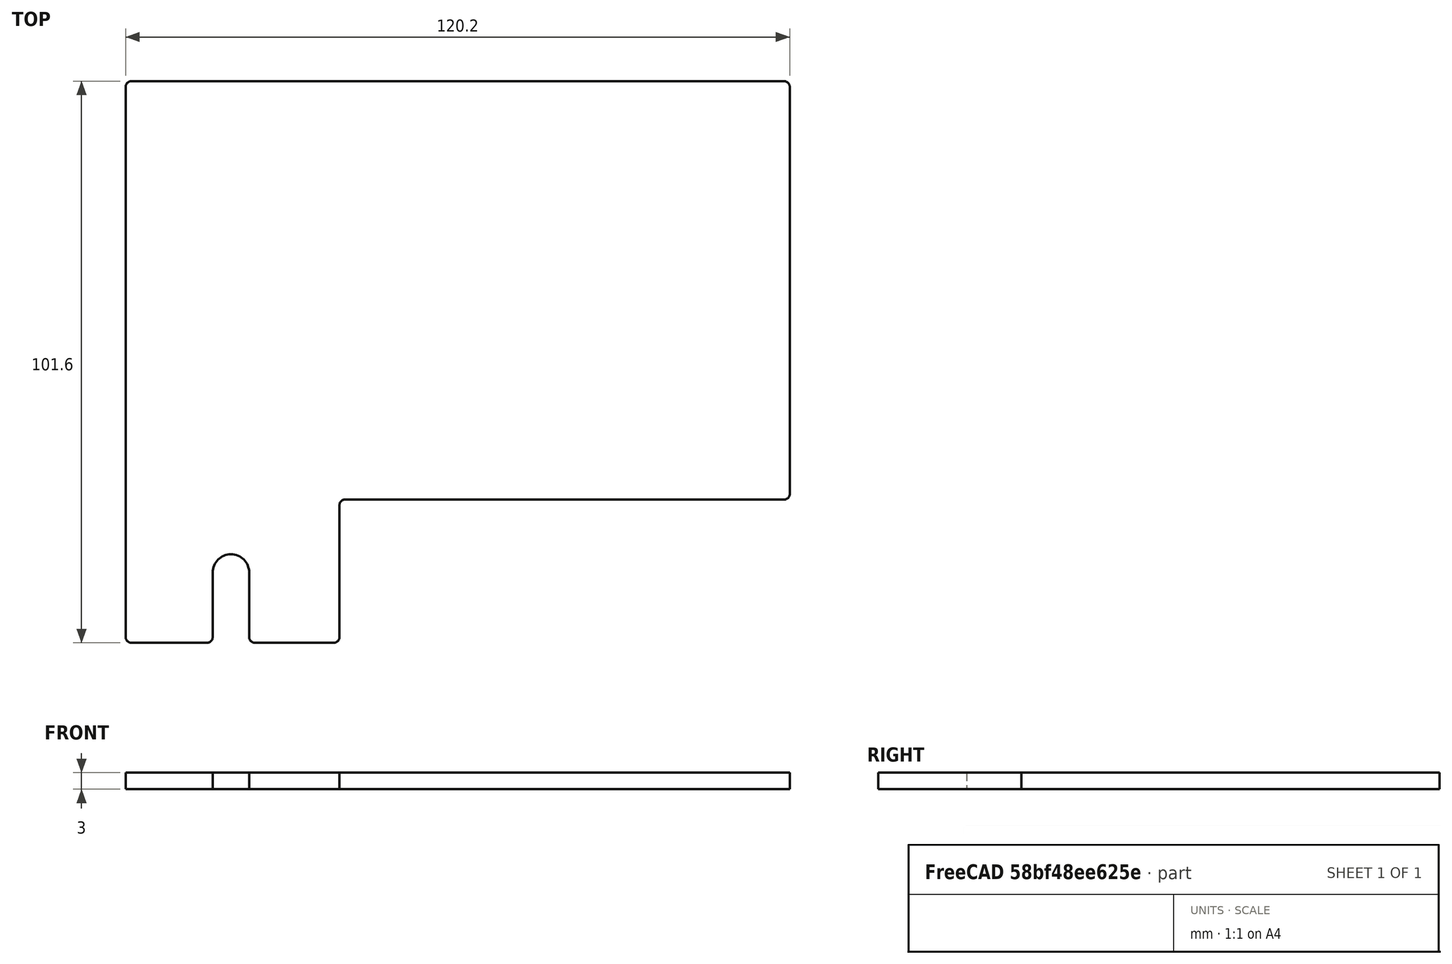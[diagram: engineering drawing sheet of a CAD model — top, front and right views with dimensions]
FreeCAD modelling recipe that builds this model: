
FCSTD DOCUMENT  (FreeCAD 0.21R33675 (Git))
Label: right_wall_front
License: All rights reserved
LicenseURL: http://en.wikipedia.org/wiki/All_rights_reserved
objects: Spreadsheet::Sheet×1, Sketcher::SketchObject×1, PartDesign::Pad×1, PartDesign::Body×1
note: 4 computed .brp shape members not serialized (recipe doc carries the construction recipe); baked Part::Feature solids carry a one-line shape summary decoded from their .brp

FEATURE [Spreadsheet::Sheet] Spreadsheet
  cells = A2='Parameters; A3='Thickness; B3(Thickness)==3 mm; A4='BeamLength; B4(BeamLength)==18 in; A5='BracketLength; B5(BracketLength)==108.6 mm; A6='DistanceLeftBracketEdgeToDoor; B6(DistanceLeftBracketEdgeToDoor)==82.4999 mm; A7='DistanceRightBracketEdgeToDoor; B7(DistanceRightBracketEdgeToDoor)==23.1001 mm; A8='ServoOffsetFromCenter; B8(ServoOffsetFromCenter)==3 in + 1 * (DistanceLeftBracketEdgeToDoor - DistanceRightBracketEdgeToDoor); A9='DoorMargin; B9(DoorMargin)==1 mm; A10='LengthMargin; B10(LengthMargin)==0 mm; A11='LengthLeftBracketEdgeToDoorGap; B11(LengthLeftBracketEdgeToDoorGap)==DistanceLeftBracketEdgeToDoor - DoorMargin; A12='LengthRightBracketEdgeToDoorGap; B12(LengthRightBracketEdgeToDoorGap)==DistanceRightBracketEdgeToDoor - DoorMargin; A13='LengthDoorGap; B13(LengthDoorGap)==BracketLength - LengthLeftBracketEdgeToDoorGap - LengthRightBracketEdgeToDoorGap; A14='BeamLengthMinusBracketLength; B14(BeamLengthMinusBracketLength)==BeamLength - BracketLength; A15='DistanceFrontToDoor; B15(DistanceFrontToDoor)==0.5 * BeamLengthMinusBracketLength + LengthLeftBracketEdgeToDoorGap - ServoOffsetFromCenter; A16='DistanceFrontToBracket; B16(DistanceFrontToBracket)==0.5 * BeamLengthMinusBracketLength - ServoOffsetFromCenter; A17='LengthFrontToDoor; B17(LengthFrontToDoor)==DistanceFrontToDoor - LengthMargin; A18='LengthFrontToBracket; B18(LengthFrontToBracket)==DistanceFrontToBracket - LengthMargin; A19='Height; B19(Height)==4 in; A20='CutoutMargin; B20(CutoutMargin)==0.5 mm; A21='CutoutHeight; B21(CutoutHeight)==1 in + CutoutMargin; A22='FilletRadius; B22(FilletRadius)==1 mm; A23='MountHoleDiameter; B23(MountHoleDiameter)==0.26 in; A24='MountHoleDistanceFromBottom; B24(MountHoleDistanceFromBottom)==0.5 in; A25='MountHoleSideMargin; B25(MountHoleSideMargin)==0.75 in; B27==3 in + DistanceLeftBracketEdgeToDoor + 0.5 * Thickness - 0.5 * BracketLength
FEATURE [Sketcher::SketchObject] Sketch
  FullyConstrained = true
  MapMode = 5
  Support = -> [XY_Plane]
  expr: Constraints[14] = Spreadsheet.FilletRadius
  expr: Constraints[20] = Spreadsheet.Height
  expr: Constraints[48] = Spreadsheet.MountHoleSideMargin
  expr: Constraints[68] = Spreadsheet.MountHoleDiameter
  expr: Constraints[69] = Spreadsheet.MountHoleDistanceFromBottom
  expr: Constraints[7] = Spreadsheet.LengthFrontToDoor
  expr: Constraints[8] = Spreadsheet.LengthFrontToBracket
  expr: Constraints[9] = Spreadsheet.CutoutHeight
  sketch-geometry (30):
    g0: LineSegment StartX=0 StartY=100.6 StartZ=0 EndX=0 EndY=1 EndZ=0
    g1: LineSegment StartX=1 StartY=0 StartZ=0 EndX=37.7002 EndY=0 EndZ=0
    g2: LineSegment StartX=38.7002 StartY=1 StartZ=0 EndX=38.7002 EndY=24.9 EndZ=0
    g3: LineSegment StartX=39.7002 StartY=25.9 StartZ=0 EndX=119.2 EndY=25.9 EndZ=0
    g4: LineSegment StartX=120.2 StartY=26.9 StartZ=0 EndX=120.2 EndY=100.6 EndZ=0
    g5: LineSegment StartX=119.2 StartY=101.6 StartZ=0 EndX=1 EndY=101.6 EndZ=0
    g6: ArcOfCircle CenterX=1 CenterY=100.6 CenterZ=0 NormalX=0 NormalY=0 NormalZ=1 AngleXU=0 Radius=1 StartAngle=1.5708 EndAngle=3.14159
    g7: GeomPoint X=0 Y=101.6 Z=0
    g8: ArcOfCircle CenterX=1 CenterY=1 CenterZ=0 NormalX=0 NormalY=0 NormalZ=1 AngleXU=0 Radius=1 StartAngle=3.14159 EndAngle=4.71239
    g9: GeomPoint X=0 Y=0 Z=0
    g10: ArcOfCircle CenterX=37.7002 CenterY=1 CenterZ=0 NormalX=0 NormalY=0 NormalZ=1 AngleXU=0 Radius=1 StartAngle=4.71239 EndAngle=6.28319
    g11: GeomPoint X=38.7002 Y=0 Z=0
    g12: ArcOfCircle CenterX=39.7002 CenterY=24.9 CenterZ=0 NormalX=0 NormalY=0 NormalZ=1 AngleXU=0 Radius=1 StartAngle=1.5708 EndAngle=3.14159
    g13: GeomPoint X=38.7002 Y=25.9 Z=0
    g14: ArcOfCircle CenterX=119.2 CenterY=26.9 CenterZ=0 NormalX=0 NormalY=0 NormalZ=1 AngleXU=0 Radius=1 StartAngle=4.71239 EndAngle=6.28319
    g15: GeomPoint X=120.2 Y=25.9 Z=0
    g16: ArcOfCircle CenterX=119.2 CenterY=100.6 CenterZ=0 NormalX=0 NormalY=0 NormalZ=1 AngleXU=0 Radius=1 StartAngle=3.8e-15 EndAngle=1.5708
    g17: GeomPoint X=120.2 Y=101.6 Z=0
    g18: GeomPoint X=19.3501 Y=0 Z=0
    g19: LineSegment StartX=19.05 StartY=0 StartZ=0 EndX=19.05 EndY=12.7 EndZ=0
    g20: Circle CenterX=19.05 CenterY=12.7 CenterZ=0 NormalX=0 NormalY=0 NormalZ=1 AngleXU=0 Radius=3.302
    g21: LineSegment StartX=19.05 StartY=12.7 StartZ=0 EndX=0 EndY=12.7 EndZ=0
    g22: ArcOfCircle CenterX=19.05 CenterY=12.7 CenterZ=0 NormalX=0 NormalY=0 NormalZ=1 AngleXU=0 Radius=3.302 StartAngle=0 EndAngle=3.14159
    g23: LineSegment StartX=19.05 StartY=12.7 StartZ=0 EndX=22.352 EndY=12.7 EndZ=0
    g24: LineSegment StartX=15.748 StartY=12.7 StartZ=0 EndX=15.748 EndY=1 EndZ=0
    g25: LineSegment StartX=22.352 StartY=12.7 StartZ=0 EndX=22.352 EndY=1 EndZ=0
    g26: ArcOfCircle CenterX=14.748 CenterY=1 CenterZ=0 NormalX=0 NormalY=0 NormalZ=1 AngleXU=0 Radius=1 StartAngle=4.71239 EndAngle=6.28319
    g27: ArcOfCircle CenterX=23.352 CenterY=1 CenterZ=0 NormalX=0 NormalY=0 NormalZ=1 AngleXU=0 Radius=1 StartAngle=3.14159 EndAngle=4.71239
    g28: LineSegment StartX=1 StartY=0 StartZ=0 EndX=14.748 EndY=0 EndZ=0
    g29: LineSegment StartX=23.352 StartY=0 StartZ=0 EndX=37.7002 EndY=0 EndZ=0
  constraints (71):
    c: Vertical(g0)
    c: Horizontal(g1)
    c: Vertical(g2)
    c: Horizontal(g3)
    c: Vertical(g4)
    c: Horizontal(g5)
    c: Coincident(g-1,g9)
    c: DistanceX(g7,g17) = 120.2
    c: DistanceX(g9,g11) = 38.7002
    c: DistanceY(g11,g13) = 25.9
    c: PointOnObject(g7,g0)
    c: PointOnObject(g7,g5)
    c: Tangent(g0,g6) = -1.5708
    c: Tangent(g5,g6) = -1.5708
    c: Radius(g6) = 1
    c: PointOnObject(g9,g0)
    c: PointOnObject(g9,g1)
    c: Tangent(g0,g8) = -1.5708
    c: Tangent(g1,g8) = -1.5708
    c: Equal(g8,g6)
    c: DistanceY(g1,g5) = 101.6
    c: PointOnObject(g11,g1)
    c: PointOnObject(g11,g2)
    c: Tangent(g1,g10) = -1.5708
    c: Tangent(g2,g10) = -1.5708
    c: Equal(g10,g8)
    c: PointOnObject(g13,g2)
    c: PointOnObject(g13,g3)
    c: Tangent(g2,g12) = 1.5708
    c: Tangent(g3,g12) = 1.5708
    c: Equal(g12,g10)
    c: PointOnObject(g15,g3)
    c: PointOnObject(g15,g4)
    c: Tangent(g3,g14) = -1.5708
    c: Tangent(g4,g14) = -1.5708
    c: Equal(g14,g12)
    c: PointOnObject(g17,g5)
    c: PointOnObject(g17,g4)
    c: Tangent(g5,g16) = -1.5708
    c: Tangent(g4,g16) = -1.5708
    c: Equal(g16,g14)
    c: Symmetric(g1,g1,g18)
    c: Vertical(g19)
    c: PointOnObject(g19,g1)
    c: Coincident(g20,g19)
    c: Coincident(g21,g20)
    c: PointOnObject(g21,g0)
    c: Horizontal(g21)
    c: DistanceX(g21,g21) = 19.05
    c: Coincident(g22,g19)
    c: PointOnObject(g22,g21)
    c: Coincident(g23,g22)
    c: Coincident(g23,g22)
    c: Horizontal(g23)
    c: PointOnObject(g22,g20)
    c: Coincident(g24,g22)
    c: Vertical(g24)
    c: Coincident(g25,g22)
    c: Vertical(g25)
    c: Equal(g24,g25)
    c: Tangent(g26,g24) = 1.5708
    c: Tangent(g26,g1) = -1.5708
    c: Tangent(g27,g25) = -1.5708
    c: Tangent(g27,g1) = -1.5708
    c: Equal(g26,g8)
    c: Coincident(g28,g8)
    c: Coincident(g28,g26)
    c: Coincident(g29,g27)
    c: Diameter(g22) = 6.604
    c: DistanceY(g26,g22) = 12.7
    c: Coincident(g29,g10)
FEATURE [PartDesign::Pad] Pad
  Direction = (0,0,1)
  Length = 3
  Length2 = 10
  Profile = -> Sketch
  ReferenceAxis = -> Sketch [N_Axis]
  Type = 0
  expr: Length = Spreadsheet.Thickness
FEATURE [PartDesign::Body] Body
  Group = -> [Sketch,Pad]
  Origin = -> Origin
  Tip = -> Pad
